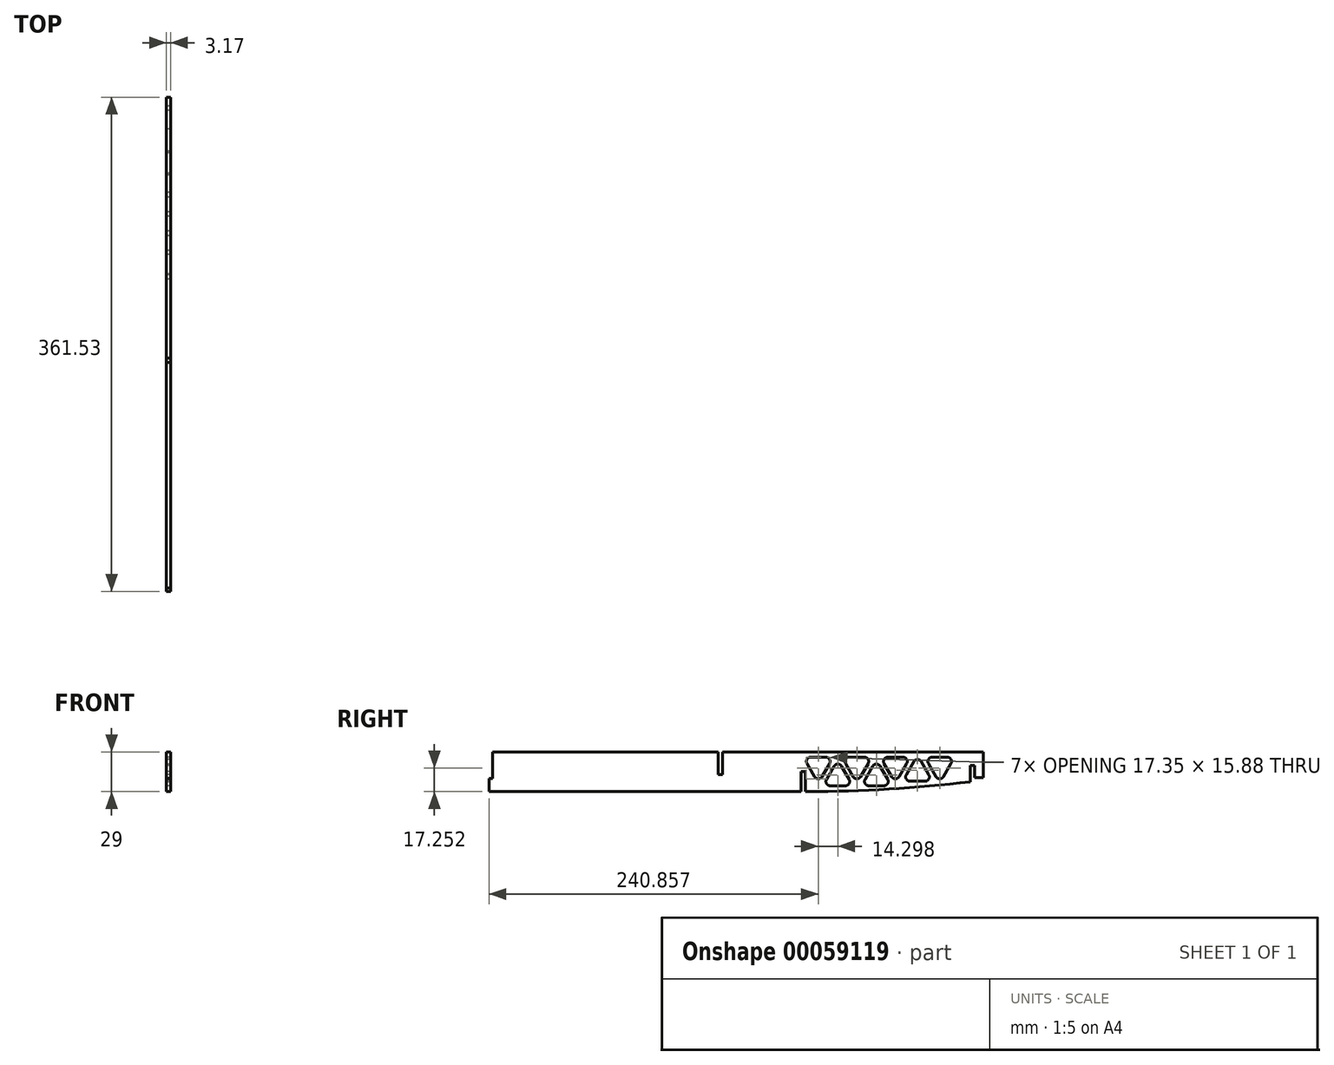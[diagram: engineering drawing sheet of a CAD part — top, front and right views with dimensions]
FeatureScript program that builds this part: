
annotation { "Feature Type Name" : "Feature", "Feature Type Description" : "" }
export const myFeature = defineFeature(function(context is Context, id is Id, definition is map)
    precondition{}
    {
        {
            var Q0;
            Q0=qCreatedBy(makeId("Right.planeOp"),FACE);
            var sketch = newSketch(context, id + "F0", { "sketchPlane" : qUnion([Q0])});
            skLineSegment(sketch, "E0", {"start": v(-248.26, 63.84) * mm, "end": v(234.34, 63.84) * mm, "construction": true});
            skLineSegment(sketch, "E1", {"start": v(-144.3, -58.57) * mm, "end": v(-144.3, -75.08) * mm});
            skLineSegment(sketch, "E2", {"start": v(-144.3, -75.08) * mm, "end": v(-147.5, -75.08) * mm});
            skLineSegment(sketch, "E3", {"start": v(-147.5, -75.08) * mm, "end": v(-147.5, -87.57) * mm, "construction": true});
            skLineSegment(sketch, "E4", {"start": v(-315.14, -87.57) * mm, "end": v(-86.77, -87.57) * mm});
            skLineSegment(sketch, "E5", {"start": v(-86.77, -87.57) * mm, "end": v(-86.77, -72.96) * mm});
            skLineSegment(sketch, "E6", {"start": v(-86.77, -72.96) * mm, "end": v(-83.57, -72.96) * mm});
            skLineSegment(sketch, "E7", {"start": v(-83.57, -72.96) * mm, "end": v(-83.57, -87.57) * mm});
            skLineSegment(sketch, "E8", {"start": v(-83.57, -87.57) * mm, "end": v(-82.1, -87.57) * mm});
            skPoint(sketch, "E9.endSnap0", {"position": v(-147.5, -81.32) * mm});
            skLineSegment(sketch, "E10", {"start": v(36.84, -68.56) * mm, "end": v(40.04, -68.56) * mm});
            skLineSegment(sketch, "E11", {"start": v(38.16, -68.56) * mm, "end": v(38.16, -58.57) * mm, "construction": true});
            skLineSegment(sketch, "E12", {"start": v(46.4, -58.57) * mm, "end": v(-144.3, -58.57) * mm});
            skLineSegment(sketch, "E13", {"start": v(-315.14, -87.57) * mm, "end": v(-315.14, -78.1) * mm});
            skLineSegment(sketch, "E14", {"start": v(-315.14, -78.1) * mm, "end": v(-312.6, -78.1) * mm});
            skLineSegment(sketch, "E15", {"start": v(-312.6, -78.1) * mm, "end": v(-312.6, -58.57) * mm});
            skLineSegment(sketch, "E16", {"start": v(-312.6, -58.57) * mm, "end": v(-147.5, -58.57) * mm});
            skLineSegment(sketch, "E17", {"start": v(-147.5, -58.57) * mm, "end": v(-147.5, -75.08) * mm});
            skLineSegment(sketch, "E18", {"start": v(36.84, -68.56) * mm, "end": v(36.84, -80.42) * mm});
            skArc(sketch, "E19", {"start": v(-82.1, -87.57) * mm, "mid": v(-22.52, -85.78) * mm, "end": v(36.84, -80.42) * mm});
            skLineSegment(sketch, "E20", {"start": v(40.04, -68.56) * mm, "end": v(40.04, -77.45) * mm});
            skLineSegment(sketch, "E21", {"start": v(40.04, -77.45) * mm, "end": v(46.4, -77.45) * mm});
            skLineSegment(sketch, "E22", {"start": v(46.4, -77.45) * mm, "end": v(46.4, -58.57) * mm});
            skPoint(sketch, "E23.orphan", {"position": v(39.68, -58.57) * mm});
            skCircle(sketch, "E24.cCircle", {"center": v(-74.28, -68.73) * mm, "radius": 12.7 * mm, "construction": true});
            skLineSegment(sketch, "E24.0", {"start": v(-66.03, -67.14) * mm, "end": v(-71.53, -76.67) * mm});
            skLineSegment(sketch, "E24.1", {"start": v(-77.03, -76.67) * mm, "end": v(-82.53, -67.14) * mm});
            skLineSegment(sketch, "E24.2", {"start": v(-79.78, -62.38) * mm, "end": v(-68.78, -62.38) * mm});
            skPoint(sketch, "E25.visualSharp", {"position": v(-85.28, -62.38) * mm});
            skArc(sketch, "E25.filletArc", {"start": v(-79.78, -62.38) * mm, "mid": v(-82.53, -63.97) * mm, "end": v(-82.53, -67.14) * mm});
            skPoint(sketch, "E26.visualSharp", {"position": v(-63.28, -62.38) * mm});
            skArc(sketch, "E26.filletArc", {"start": v(-66.03, -67.14) * mm, "mid": v(-66.03, -63.97) * mm, "end": v(-68.78, -62.38) * mm});
            skPoint(sketch, "E27.visualSharp", {"position": v(-74.28, -81.43) * mm});
            skArc(sketch, "E27.filletArc", {"start": v(-77.03, -76.67) * mm, "mid": v(-74.28, -78.26) * mm, "end": v(-71.53, -76.67) * mm});
            skLineSegment(sketch, "E28.0", {"start": v(-65.4, -69.84) * mm, "end": v(-73.64, -84.13) * mm, "construction": true});
            skArc(sketch, "E29.MirrorCS", {"start": v(-65.48, -83.34) * mm, "mid": v(-68.23, -81.75) * mm, "end": v(-68.23, -78.57) * mm});
            skLineSegment(sketch, "E30.MirrorCS", {"start": v(-65.48, -83.34) * mm, "end": v(-54.49, -83.34) * mm});
            skArc(sketch, "E31.MirrorCS", {"start": v(-51.74, -78.57) * mm, "mid": v(-51.74, -81.75) * mm, "end": v(-54.49, -83.34) * mm});
            skLineSegment(sketch, "E32.MirrorCS", {"start": v(-62.73, -69.05) * mm, "end": v(-68.23, -78.57) * mm});
            skLineSegment(sketch, "E33.MirrorCS", {"start": v(-51.74, -78.57) * mm, "end": v(-57.24, -69.05) * mm});
            skArc(sketch, "E34.MirrorCS", {"start": v(-62.73, -69.05) * mm, "mid": v(-59.98, -67.46) * mm, "end": v(-57.24, -69.05) * mm});
            skLineSegment(sketch, "E35.1.0.0", {"start": v(-51.57, -62.38) * mm, "end": v(-40.57, -62.38) * mm});
            skArc(sketch, "E35.1.0.1", {"start": v(-51.57, -62.38) * mm, "mid": v(-54.32, -63.97) * mm, "end": v(-54.32, -67.14) * mm});
            skLineSegment(sketch, "E35.1.0.2", {"start": v(-48.82, -76.67) * mm, "end": v(-54.32, -67.14) * mm});
            skArc(sketch, "E35.1.0.3", {"start": v(-48.82, -76.67) * mm, "mid": v(-46.07, -78.26) * mm, "end": v(-43.32, -76.67) * mm});
            skLineSegment(sketch, "E35.1.0.4", {"start": v(-37.82, -67.14) * mm, "end": v(-43.32, -76.67) * mm});
            skArc(sketch, "E35.1.0.5", {"start": v(-37.82, -67.14) * mm, "mid": v(-37.82, -63.97) * mm, "end": v(-40.57, -62.38) * mm});
            skArc(sketch, "E35.1.0.6", {"start": v(-34.52, -69.05) * mm, "mid": v(-31.77, -67.46) * mm, "end": v(-29.02, -69.05) * mm});
            skLineSegment(sketch, "E35.1.0.7", {"start": v(-34.52, -69.05) * mm, "end": v(-40.02, -78.57) * mm});
            skArc(sketch, "E35.1.0.8", {"start": v(-37.27, -83.34) * mm, "mid": v(-40.02, -81.75) * mm, "end": v(-40.02, -78.57) * mm});
            skLineSegment(sketch, "E35.1.0.9", {"start": v(-37.27, -83.34) * mm, "end": v(-26.27, -83.34) * mm});
            skArc(sketch, "E35.1.0.10", {"start": v(-23.52, -78.57) * mm, "mid": v(-23.52, -81.75) * mm, "end": v(-26.27, -83.34) * mm});
            skLineSegment(sketch, "E35.1.0.11", {"start": v(-23.52, -78.57) * mm, "end": v(-29.02, -69.05) * mm});
            skLineSegment(sketch, "E35.2.0.0", {"start": v(-23.35, -62.38) * mm, "end": v(-12.36, -62.38) * mm});
            skArc(sketch, "E35.2.0.1", {"start": v(-23.35, -62.38) * mm, "mid": v(-26.1, -63.97) * mm, "end": v(-26.1, -67.14) * mm});
            skLineSegment(sketch, "E35.2.0.2", {"start": v(-20.6, -76.67) * mm, "end": v(-26.1, -67.14) * mm});
            skArc(sketch, "E35.2.0.3", {"start": v(-20.6, -76.67) * mm, "mid": v(-17.85, -78.26) * mm, "end": v(-15.1, -76.67) * mm});
            skLineSegment(sketch, "E35.2.0.4", {"start": v(-9.6, -67.14) * mm, "end": v(-15.1, -76.67) * mm});
            skArc(sketch, "E35.2.0.5", {"start": v(-9.6, -67.14) * mm, "mid": v(-9.6, -63.97) * mm, "end": v(-12.36, -62.38) * mm});
            skLineSegment(sketch, "E35.direction1", {"start": v(-79.78, -62.38) * mm, "end": v(-51.57, -62.38) * mm, "construction": true});
            skCircle(sketch, "E36.cCircle", {"center": v(-1.64, -73.67) * mm, "radius": 12.7 * mm, "construction": true});
            skLineSegment(sketch, "E36.0", {"start": v(3.86, -80.02) * mm, "end": v(-7.14, -80.02) * mm});
            skLineSegment(sketch, "E36.1", {"start": v(-9.9, -75.26) * mm, "end": v(-4.4, -65.73) * mm});
            skLineSegment(sketch, "E36.2", {"start": v(1.1, -65.73) * mm, "end": v(6.6, -75.26) * mm});
            skPoint(sketch, "E37.visualSharp", {"position": v(-1.64, -60.97) * mm});
            skArc(sketch, "E37.filletArc", {"start": v(1.1, -65.73) * mm, "mid": v(-1.64, -64.14) * mm, "end": v(-4.4, -65.73) * mm});
            skPoint(sketch, "E38.visualSharp", {"position": v(-12.64, -80.02) * mm});
            skArc(sketch, "E38.filletArc", {"start": v(-9.9, -75.26) * mm, "mid": v(-9.9, -78.43) * mm, "end": v(-7.14, -80.02) * mm});
            skPoint(sketch, "E39.visualSharp", {"position": v(9.36, -80.02) * mm});
            skArc(sketch, "E39.filletArc", {"start": v(3.86, -80.02) * mm, "mid": v(6.6, -78.43) * mm, "end": v(6.6, -75.26) * mm});
            skCircle(sketch, "E40.cCircle", {"center": v(14.57, -68.73) * mm, "radius": 12.7 * mm, "construction": true});
            skLineSegment(sketch, "E40.0", {"start": v(9.07, -62.38) * mm, "end": v(20.07, -62.38) * mm});
            skLineSegment(sketch, "E40.1", {"start": v(22.82, -67.14) * mm, "end": v(17.32, -76.67) * mm});
            skLineSegment(sketch, "E40.2", {"start": v(11.82, -76.67) * mm, "end": v(6.32, -67.14) * mm});
            skPoint(sketch, "E41.visualSharp", {"position": v(3.57, -62.38) * mm});
            skArc(sketch, "E41.filletArc", {"start": v(9.07, -62.38) * mm, "mid": v(6.32, -63.97) * mm, "end": v(6.32, -67.14) * mm});
            skPoint(sketch, "E42.visualSharp", {"position": v(25.57, -62.38) * mm});
            skArc(sketch, "E42.filletArc", {"start": v(22.82, -67.14) * mm, "mid": v(22.82, -63.97) * mm, "end": v(20.07, -62.38) * mm});
            skPoint(sketch, "E43.visualSharp", {"position": v(14.57, -81.43) * mm});
            skArc(sketch, "E43.filletArc", {"start": v(11.82, -76.67) * mm, "mid": v(14.57, -78.26) * mm, "end": v(17.32, -76.67) * mm});
            skSolve(sketch);
        }
        {
            var Q0;
            Q0 = qSketchRegion(id + "F0", true);
            extrude(context, id + "F1", {"entities" : qUnion([Q0]), "depth" : 3.17 * mm});
        }
    });
